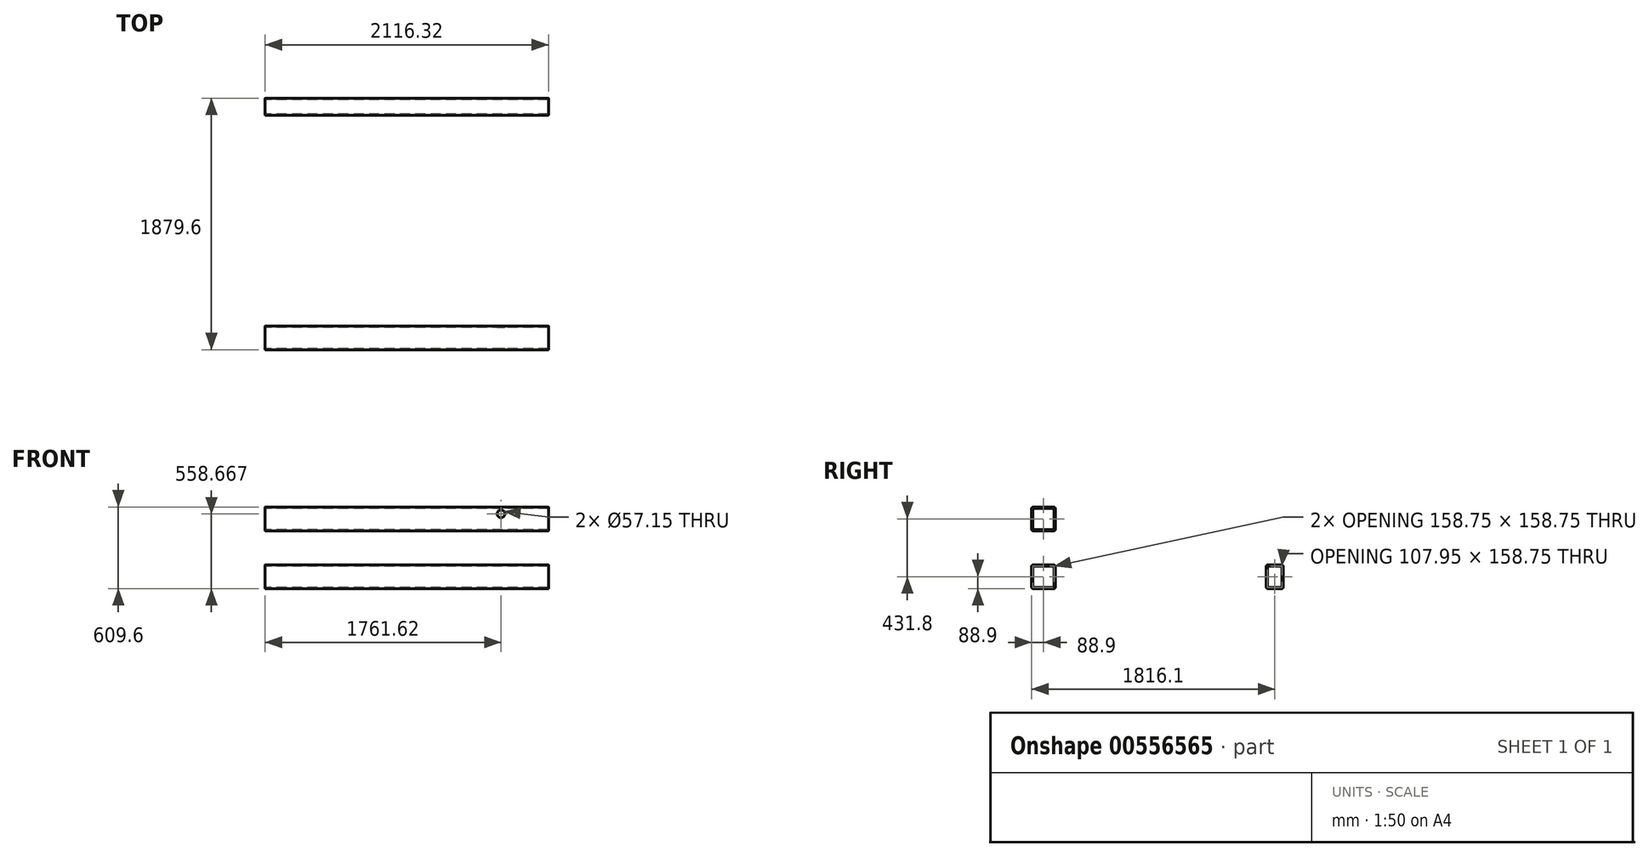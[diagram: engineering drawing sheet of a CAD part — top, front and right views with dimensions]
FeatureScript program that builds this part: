
annotation { "Feature Type Name" : "Feature", "Feature Type Description" : "" }
export const myFeature = defineFeature(function(context is Context, id is Id, definition is map)
    precondition{}
    {
        {
            var Q0;
            Q0=qCreatedBy(makeId("Right.planeOp"),FACE);
            var sketch = newSketch(context, id + "F0", { "sketchPlane" : qUnion([Q0])});
            skLineSegment(sketch, "E0.bottom", {"start": v(-76.2, -88.9) * mm, "end": v(76.2, -88.9) * mm});
            skLineSegment(sketch, "E0.top", {"start": v(-76.2, 88.9) * mm, "end": v(76.2, 88.9) * mm});
            skLineSegment(sketch, "E0.left", {"start": v(-88.9, -76.2) * mm, "end": v(-88.9, 76.2) * mm});
            skLineSegment(sketch, "E0.right", {"start": v(88.9, -76.2) * mm, "end": v(88.9, 76.2) * mm});
            skPoint(sketch, "E1.visualSharp", {"position": v(-88.9, 88.9) * mm});
            skArc(sketch, "E1.filletArc", {"start": v(-76.2, 88.9) * mm, "mid": v(-85.18, 85.18) * mm, "end": v(-88.9, 76.2) * mm});
            skPoint(sketch, "E2.visualSharp", {"position": v(88.9, 88.9) * mm});
            skArc(sketch, "E2.filletArc", {"start": v(88.9, 76.2) * mm, "mid": v(85.18, 85.18) * mm, "end": v(76.2, 88.9) * mm});
            skPoint(sketch, "E3.visualSharp", {"position": v(88.9, -88.9) * mm});
            skArc(sketch, "E3.filletArc", {"start": v(76.2, -88.9) * mm, "mid": v(85.18, -85.18) * mm, "end": v(88.9, -76.2) * mm});
            skPoint(sketch, "E4.visualSharp", {"position": v(-88.9, -88.9) * mm});
            skArc(sketch, "E4.filletArc", {"start": v(-88.9, -76.2) * mm, "mid": v(-85.18, -85.18) * mm, "end": v(-76.2, -88.9) * mm});
            skLineSegment(sketch, "E5.0", {"start": v(-76.2, 79.38) * mm, "end": v(76.2, 79.38) * mm});
            skArc(sketch, "E5.1", {"start": v(79.37, 76.2) * mm, "mid": v(78.45, 78.45) * mm, "end": v(76.2, 79.38) * mm});
            skArc(sketch, "E5.2", {"start": v(-76.2, 79.38) * mm, "mid": v(-78.45, 78.45) * mm, "end": v(-79.37, 76.2) * mm});
            skLineSegment(sketch, "E5.3", {"start": v(79.37, -76.2) * mm, "end": v(79.37, 76.2) * mm});
            skLineSegment(sketch, "E5.4", {"start": v(-79.37, -76.2) * mm, "end": v(-79.37, 76.2) * mm});
            skArc(sketch, "E5.5", {"start": v(-79.37, -76.2) * mm, "mid": v(-78.45, -78.45) * mm, "end": v(-76.2, -79.38) * mm});
            skLineSegment(sketch, "E5.6", {"start": v(-76.2, -79.38) * mm, "end": v(76.2, -79.38) * mm});
            skArc(sketch, "E5.7", {"start": v(76.2, -79.38) * mm, "mid": v(78.45, -78.45) * mm, "end": v(79.37, -76.2) * mm});
            skSolve(sketch);
        }
        {
            var Q0;
            Q0 = qSketchRegion(id + "F0", true);
            extrude(context, id + "F1", {"entities" : qUnion([Q0]), "endBound" : BoundingType.SYMMETRIC, "depth" : 2116.33 * mm, "offsetDistance" : 25.4 * mm});
        }
        {
            var Q0;
            Q0=qCreatedBy(makeId("Right.planeOp"),FACE);
            var sketch = newSketch(context, id + "F2", { "sketchPlane" : qUnion([Q0])});
            skLineSegment(sketch, "E6.bottom", {"start": v(-76.2, 342.9) * mm, "end": v(76.2, 342.9) * mm});
            skLineSegment(sketch, "E6.top", {"start": v(-76.2, 520.7) * mm, "end": v(76.2, 520.7) * mm});
            skLineSegment(sketch, "E6.left", {"start": v(-88.9, 355.6) * mm, "end": v(-88.9, 508) * mm});
            skLineSegment(sketch, "E6.right", {"start": v(88.9, 355.6) * mm, "end": v(88.9, 508) * mm});
            skPoint(sketch, "E7.visualSharp", {"position": v(-88.9, 520.7) * mm});
            skArc(sketch, "E7.filletArc", {"start": v(-76.2, 520.7) * mm, "mid": v(-85.18, 516.98) * mm, "end": v(-88.9, 508) * mm});
            skPoint(sketch, "E8.visualSharp", {"position": v(88.9, 520.7) * mm});
            skArc(sketch, "E8.filletArc", {"start": v(88.9, 508) * mm, "mid": v(85.18, 516.98) * mm, "end": v(76.2, 520.7) * mm});
            skPoint(sketch, "E9.visualSharp", {"position": v(88.9, 342.9) * mm});
            skArc(sketch, "E9.filletArc", {"start": v(76.2, 342.9) * mm, "mid": v(85.18, 346.62) * mm, "end": v(88.9, 355.6) * mm});
            skPoint(sketch, "E10.visualSharp", {"position": v(-88.9, 342.9) * mm});
            skArc(sketch, "E10.filletArc", {"start": v(-88.9, 355.6) * mm, "mid": v(-85.18, 346.62) * mm, "end": v(-76.2, 342.9) * mm});
            skLineSegment(sketch, "E11.0", {"start": v(-76.2, 511.17) * mm, "end": v(76.2, 511.17) * mm});
            skArc(sketch, "E11.1", {"start": v(79.37, 508) * mm, "mid": v(78.45, 510.25) * mm, "end": v(76.2, 511.17) * mm});
            skArc(sketch, "E11.2", {"start": v(-76.2, 511.17) * mm, "mid": v(-78.45, 510.25) * mm, "end": v(-79.38, 508) * mm});
            skLineSegment(sketch, "E11.3", {"start": v(79.37, 355.6) * mm, "end": v(79.37, 508) * mm});
            skLineSegment(sketch, "E11.4", {"start": v(-79.38, 355.6) * mm, "end": v(-79.38, 508) * mm});
            skArc(sketch, "E11.5", {"start": v(-79.38, 355.6) * mm, "mid": v(-78.45, 353.35) * mm, "end": v(-76.2, 352.43) * mm});
            skLineSegment(sketch, "E11.6", {"start": v(-76.2, 352.43) * mm, "end": v(76.2, 352.43) * mm});
            skArc(sketch, "E11.7", {"start": v(76.2, 352.43) * mm, "mid": v(78.45, 353.35) * mm, "end": v(79.37, 355.6) * mm});
            skSolve(sketch);
        }
        {
            var Q0;
            Q0 = qSketchRegion(id + "F2", true);
            extrude(context, id + "F3", {"entities" : qUnion([Q0]), "endBound" : BoundingType.SYMMETRIC, "depth" : 2116.33 * mm, "offsetDistance" : 25.4 * mm});
        }
        {
            var Q0;
            Q0=makeQuery(id+"F3.opExtrude","SWEPT_FACE",FACE,{"disambiguationData":[OSD([sQuery(id+"F2.wireOp",EDGE,"E6.left")])]});
            var sketch = newSketch(context, id + "F4", { "sketchPlane" : qUnion([Q0])});
            skCircle(sketch, "E12", {"center": v(703.46, 469.77) * mm, "radius": 28.58 * mm});
            skPoint(sketch, "E13", {"position": v(-1058.16, 431.8) * mm});
            skPoint(sketch, "E14", {"position": v(1058.16, 431.8) * mm});
            skSolve(sketch);
        }
        {
            var Q0;
            Q0 = qSketchRegion(id + "F4", true);
            extrude(context, id + "F5", {"entities" : qUnion([Q0]), "operationType" : NewBodyOperationType.REMOVE, "endBound" : BoundingType.THROUGH_ALL, "oppositeDirection" : true, "depth" : 25.4 * mm, "offsetDistance" : 25.4 * mm});
        }
        {
            var Q0;
            Q0=qCreatedBy(makeId("Right.planeOp"),FACE);
            var sketch = newSketch(context, id + "F6", { "sketchPlane" : qUnion([Q0])});
            skLineSegment(sketch, "E15.bottom", {"start": v(1676.4, -88.9) * mm, "end": v(1778, -88.9) * mm});
            skLineSegment(sketch, "E15.top", {"start": v(1676.4, 88.9) * mm, "end": v(1778, 88.9) * mm});
            skLineSegment(sketch, "E15.left", {"start": v(1663.7, -76.2) * mm, "end": v(1663.7, 76.2) * mm});
            skLineSegment(sketch, "E15.right", {"start": v(1790.7, -76.2) * mm, "end": v(1790.7, 76.2) * mm});
            skPoint(sketch, "E16.visualSharp", {"position": v(1663.7, 88.9) * mm});
            skArc(sketch, "E16.filletArc", {"start": v(1676.4, 88.9) * mm, "mid": v(1667.42, 85.18) * mm, "end": v(1663.7, 76.2) * mm});
            skPoint(sketch, "E17.visualSharp", {"position": v(1790.7, 88.9) * mm});
            skArc(sketch, "E17.filletArc", {"start": v(1790.7, 76.2) * mm, "mid": v(1786.98, 85.18) * mm, "end": v(1778, 88.9) * mm});
            skPoint(sketch, "E18.visualSharp", {"position": v(1790.7, -88.9) * mm});
            skArc(sketch, "E18.filletArc", {"start": v(1778, -88.9) * mm, "mid": v(1786.98, -85.18) * mm, "end": v(1790.7, -76.2) * mm});
            skPoint(sketch, "E19.visualSharp", {"position": v(1663.7, -88.9) * mm});
            skArc(sketch, "E19.filletArc", {"start": v(1663.7, -76.2) * mm, "mid": v(1667.42, -85.18) * mm, "end": v(1676.4, -88.9) * mm});
            skLineSegment(sketch, "E20.0", {"start": v(1676.4, 79.38) * mm, "end": v(1778, 79.38) * mm});
            skArc(sketch, "E20.1", {"start": v(1781.18, 76.2) * mm, "mid": v(1780.25, 78.45) * mm, "end": v(1778, 79.38) * mm});
            skArc(sketch, "E20.2", {"start": v(1676.4, 79.38) * mm, "mid": v(1674.15, 78.45) * mm, "end": v(1673.23, 76.2) * mm});
            skLineSegment(sketch, "E20.3", {"start": v(1781.18, -76.2) * mm, "end": v(1781.18, 76.2) * mm});
            skLineSegment(sketch, "E20.4", {"start": v(1673.23, -76.2) * mm, "end": v(1673.23, 76.2) * mm});
            skArc(sketch, "E20.5", {"start": v(1673.23, -76.2) * mm, "mid": v(1674.15, -78.45) * mm, "end": v(1676.4, -79.37) * mm});
            skLineSegment(sketch, "E20.6", {"start": v(1676.4, -79.37) * mm, "end": v(1778, -79.37) * mm});
            skArc(sketch, "E20.7", {"start": v(1778, -79.37) * mm, "mid": v(1780.25, -78.45) * mm, "end": v(1781.18, -76.2) * mm});
            skSolve(sketch);
        }
        {
            var Q0;
            Q0 = qSketchRegion(id + "F6", true);
            extrude(context, id + "F7", {"entities" : qUnion([Q0]), "endBound" : BoundingType.SYMMETRIC, "depth" : 2116.33 * mm, "offsetDistance" : 25.4 * mm});
        }
    });
